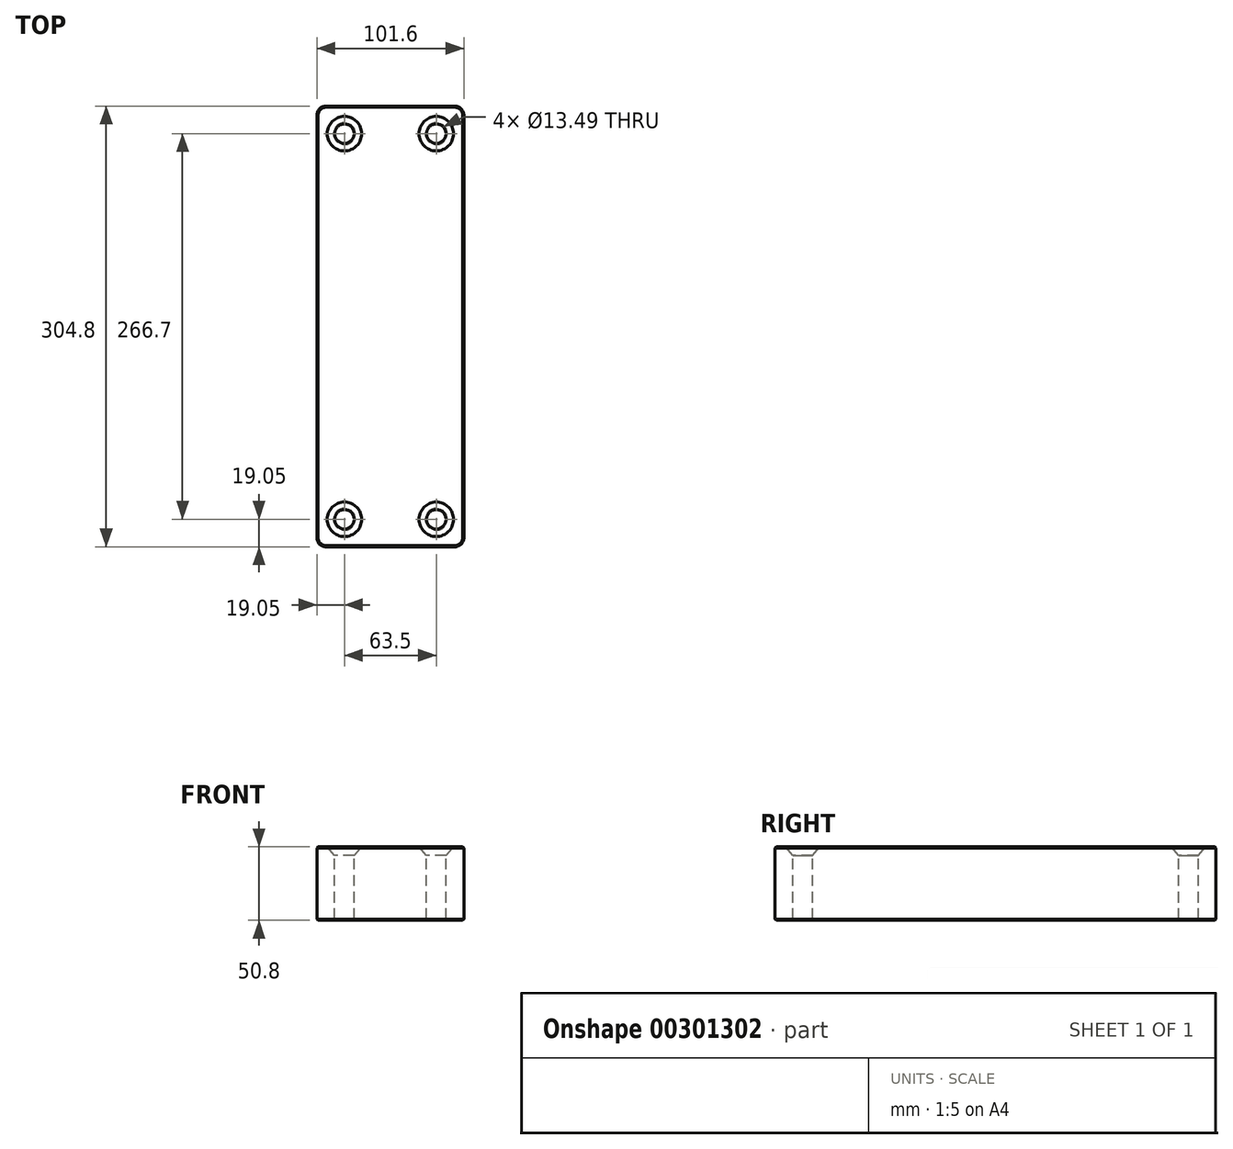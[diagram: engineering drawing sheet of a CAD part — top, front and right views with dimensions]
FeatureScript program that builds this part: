
annotation { "Feature Type Name" : "Feature", "Feature Type Description" : "" }
export const myFeature = defineFeature(function(context is Context, id is Id, definition is map)
    precondition{}
    {
        {
            var Q0;
            Q0=qCreatedBy(makeId("Front.planeOp"),FACE);
            var sketch = newSketch(context, id + "F0", { "sketchPlane" : qUnion([Q0])});
            skLineSegment(sketch, "E0.bottom", {"start": v(-50.8, -25.4) * mm, "end": v(50.8, -25.4) * mm});
            skLineSegment(sketch, "E0.top", {"start": v(-50.8, 25.4) * mm, "end": v(50.8, 25.4) * mm});
            skLineSegment(sketch, "E0.left", {"start": v(-50.8, -25.4) * mm, "end": v(-50.8, 25.4) * mm});
            skLineSegment(sketch, "E0.right", {"start": v(50.8, -25.4) * mm, "end": v(50.8, 25.4) * mm});
            skSolve(sketch);
        }
        {
            var Q0;
            Q0=makeQuery(id+"F0.imprint","IMPRINT",FACE,{"disambiguationData":[TD([[makeQuery(id+"F0.imprint","IMPRINT",EDGE,{"derivedFrom":sQuery(id+"F0.wireOp",EDGE,"E0.bottom")}),1.0]])]});
            extrude(context, id + "F1", {"entities" : qUnion([Q0]), "endBound" : BoundingType.SYMMETRIC, "depth" : 304.8 * mm});
        }
        {
            var Q0;
            Q0=makeQuery(id+"F1.opExtrude","SWEPT_FACE",FACE,{"disambiguationData":[OSD([sQuery(id+"F0.wireOp",EDGE,"E0.top")])]});
            var sketch = newSketch(context, id + "F2", { "sketchPlane" : qUnion([Q0])});
            skPoint(sketch, "E1", {"position": v(-31.75, 133.35) * mm});
            skPoint(sketch, "E2.MirrorP", {"position": v(31.75, 133.35) * mm});
            skPoint(sketch, "E3.MirrorP", {"position": v(-31.75, -133.35) * mm});
            skPoint(sketch, "E4.MirrorP", {"position": v(31.75, -133.35) * mm});
            skSolve(sketch);
        }
        {
            var Q0;
            Q0=sQuery(id+"F2.wireOp",VERTEX,"E1");
            var Q1;
            Q1=sQuery(id+"F2.wireOp",VERTEX,"E2.MirrorP");
            var Q2;
            Q2=sQuery(id+"F2.wireOp",VERTEX,"E4.MirrorP");
            var Q3;
            Q3=sQuery(id+"F2.wireOp",VERTEX,"E3.MirrorP");
            var Q4;
            Q4=makeQuery(id+"F1.opExtrude","SWEPT_BODY",BODY,{"disambiguationData":[OSD([sQuery(id+"F0.wireOp",EDGE,"E0.bottom"),sQuery(id+"F0.wireOp",EDGE,"E0.top"),sQuery(id+"F0.wireOp",EDGE,"E0.left"),sQuery(id+"F0.wireOp",EDGE,"E0.right")])]});
            hole(context, id + "F3", {"style" : HoleStyle.C_SINK, "endStyle" : HoleEndStyle.THROUGH, "standardTappedOrClearance" : lookupTablePath({ "standard" : "ANSI", "fit" : "Normal (ASME)", "size" : "1/2", "type" : "Clearance" }), "standardBlindInLast" : lookupTablePath({ "fit" : "Free", "standard" : "ANSI", "size" : "1/2", "type" : "Clearance" }), "holeDiameter" : 13.5 * mm, "cSinkDiameter" : 23.83 * mm, "cSinkAngle" : 82 * degree, "tappedDepth" : 12.7 * mm, "tapClearance" : 3, "locations" : qUnion([Q0, Q1, Q2, Q3]), "scope" : qUnion([Q4])});
        }
        {
            var Q0;
            Q0=makeQuery(id+"F1.opExtrude","CAP_EDGE",EDGE,{"disambiguationData":[OSD([sQuery(id+"F0.wireOp",EDGE,"E0.right")])],"isStart":false});
            var Q1;
            Q1=makeQuery(id+"F1.opExtrude","CAP_EDGE",EDGE,{"disambiguationData":[OSD([sQuery(id+"F0.wireOp",EDGE,"E0.right")])],"isStart":true});
            var Q2;
            Q2=makeQuery(id+"F1.opExtrude","CAP_EDGE",EDGE,{"disambiguationData":[OSD([sQuery(id+"F0.wireOp",EDGE,"E0.left")])],"isStart":false});
            var Q3;
            Q3=makeQuery(id+"F1.opExtrude","CAP_EDGE",EDGE,{"disambiguationData":[OSD([sQuery(id+"F0.wireOp",EDGE,"E0.left")])],"isStart":true});
            fillet(context, id + "F4", {"entities" : qUnion([Q0, Q1, Q2, Q3]), "radius" : 6.35 * mm, "tangentPropagation" : true, "allowEdgeOverflow" : false});
        }
        {
            var Q0;
            Q0=makeQuery(id+"F1.opExtrude","CAP_EDGE",EDGE,{"disambiguationData":[OSD([sQuery(id+"F0.wireOp",EDGE,"E0.top")])],"isStart":true});
            var Q1;
            Q1=makeQuery(id+"F1.opExtrude","SWEPT_EDGE",EDGE,{"disambiguationData":[OSD([sQuery(id+"F0.wireOp",EDGE,"E0.top"),sQuery(id+"F0.wireOp",EDGE,"E0.right")])]});
            var Q2;
            Q2=makeQuery(id+"F1.opExtrude","CAP_EDGE",EDGE,{"disambiguationData":[OSD([sQuery(id+"F0.wireOp",EDGE,"E0.top")])],"isStart":false});
            var Q3;
            Q3=makeQuery(id+"F1.opExtrude","SWEPT_EDGE",EDGE,{"disambiguationData":[OSD([sQuery(id+"F0.wireOp",EDGE,"E0.top"),sQuery(id+"F0.wireOp",EDGE,"E0.left")])]});
            var Q4;
            Q4=makeQuery(id+"F1.opExtrude","SWEPT_FACE",FACE,{"disambiguationData":[OSD([sQuery(id+"F0.wireOp",EDGE,"E0.bottom")])]});
            chamfer(context, id + "F5", {"entities" : qUnion([Q0, Q1, Q2, Q3, Q4]), "width" : 0.81 * mm, "tangentPropagation" : true});
        }
    });
